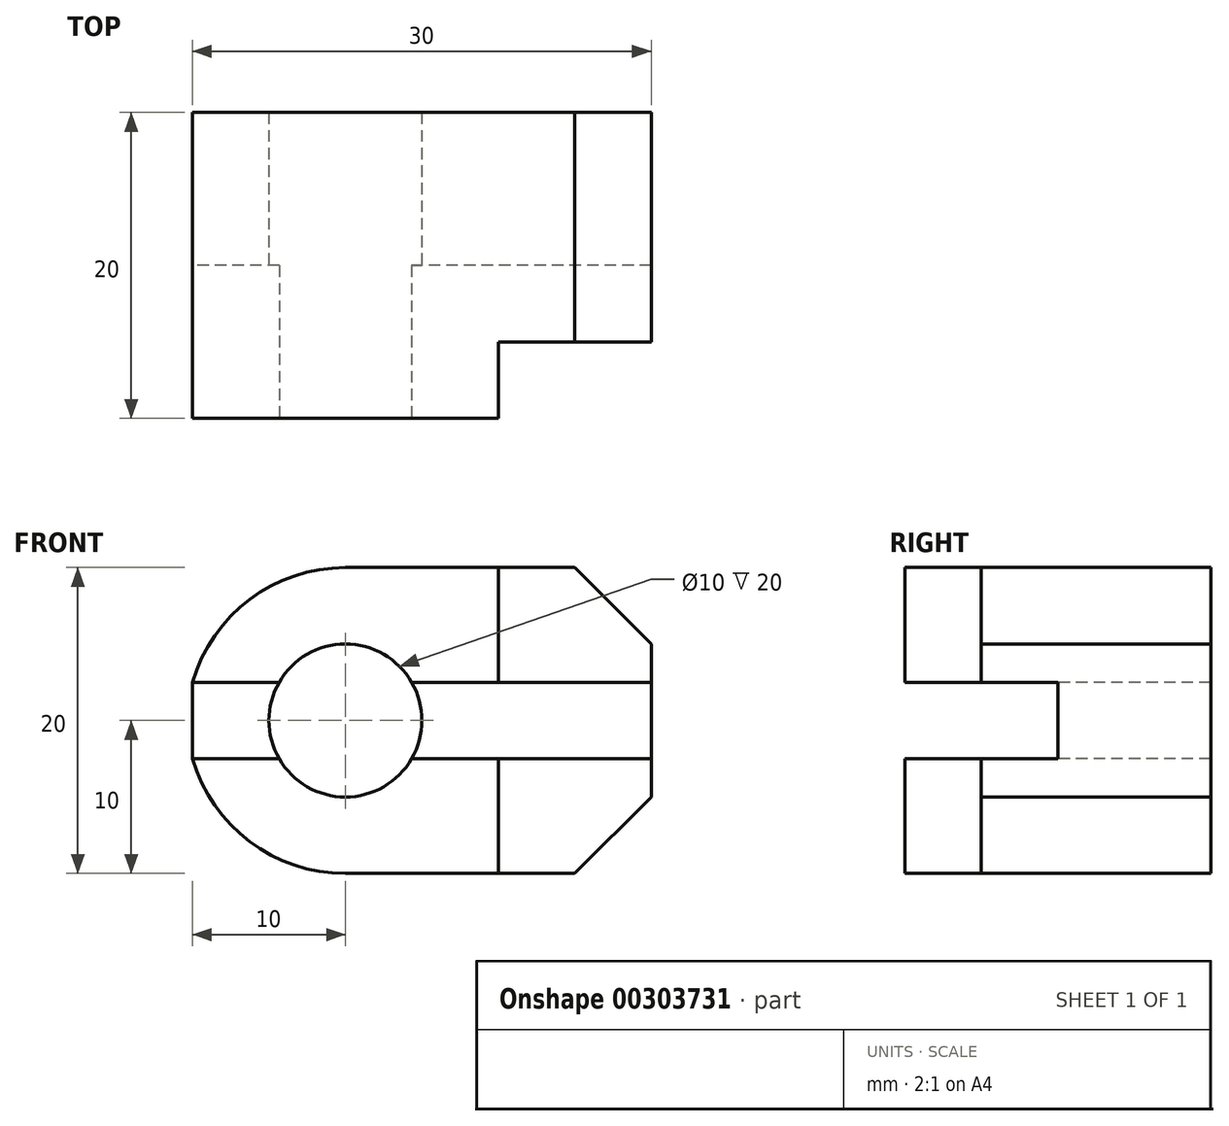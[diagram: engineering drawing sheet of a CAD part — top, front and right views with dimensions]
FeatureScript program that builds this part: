
annotation { "Feature Type Name" : "Feature", "Feature Type Description" : "" }
export const myFeature = defineFeature(function(context is Context, id is Id, definition is map)
    precondition{}
    {
        {
            var Q0;
            Q0=qCreatedBy(makeId("Top.planeOp"),FACE);
            var sketch = newSketch(context, id + "F0", { "sketchPlane" : qUnion([Q0])});
            skLineSegment(sketch, "E0", {"start": v(0, 0) * mm, "end": v(20, 0) * mm});
            skLineSegment(sketch, "E1", {"start": v(20, 0) * mm, "end": v(20, 5) * mm});
            skLineSegment(sketch, "E2", {"start": v(0, 0) * mm, "end": v(0, 20) * mm});
            skLineSegment(sketch, "E3", {"start": v(0, 20) * mm, "end": v(30, 20) * mm});
            skLineSegment(sketch, "E4", {"start": v(30, 20) * mm, "end": v(30, 5) * mm});
            skLineSegment(sketch, "E5", {"start": v(30, 5) * mm, "end": v(10, 5) * mm});
            skLineSegment(sketch, "E6", {"start": v(25, 20) * mm, "end": v(25, 5) * mm});
            skSolve(sketch);
        }
        {
            var Q0;
            Q0 = qSketchRegion(id + "F0", true);
            extrude(context, id + "F1", {"entities" : qUnion([Q0]), "endBound" : BoundingType.SYMMETRIC, "depth" : 20 * mm});
        }
        {
            var Q0;
            Q0=qCreatedBy(makeId("Front.planeOp"),FACE);
            var sketch = newSketch(context, id + "F2", { "sketchPlane" : qUnion([Q0])});
            skCircle(sketch, "E7", {"center": v(10, 0) * mm, "radius": 5 * mm});
            skPoint(sketch, "E8", {"position": v(10, 2.5) * mm});
            skPoint(sketch, "E9", {"position": v(10, -2.5) * mm});
            skLineSegment(sketch, "E10", {"start": v(5.67, 2.5) * mm, "end": v(0, 2.5) * mm});
            skLineSegment(sketch, "E11", {"start": v(5.67, -2.5) * mm, "end": v(0, -2.5) * mm});
            skLineSegment(sketch, "E12", {"start": v(14.33, 2.5) * mm, "end": v(20, 2.5) * mm});
            skLineSegment(sketch, "E13", {"start": v(14.33, -2.5) * mm, "end": v(20, -2.5) * mm});
            skLineSegment(sketch, "E14", {"start": v(14.33, 2.5) * mm, "end": v(30, 2.5) * mm});
            skLineSegment(sketch, "E15", {"start": v(14.33, -2.5) * mm, "end": v(30, -2.5) * mm});
            skArc(sketch, "E16", {"start": v(20, 2.5) * mm, "mid": v(10, 10) * mm, "end": v(0, 2.5) * mm});
            skPoint(sketch, "E17", {"position": v(10, -10) * mm});
            skArc(sketch, "E18", {"start": v(0, -2.5) * mm, "mid": v(10, -10) * mm, "end": v(20, -2.5) * mm});
            skLineSegment(sketch, "E19", {"start": v(10, 10) * mm, "end": v(0, 10) * mm});
            skLineSegment(sketch, "E20", {"start": v(0, 10) * mm, "end": v(0, 2.5) * mm});
            skLineSegment(sketch, "E21", {"start": v(10, -10) * mm, "end": v(0, -10) * mm});
            skLineSegment(sketch, "E22", {"start": v(0, -10) * mm, "end": v(0, -2.5) * mm});
            skLineSegment(sketch, "E23", {"start": v(0, 0) * mm, "end": v(35.65, 0) * mm, "construction": true});
            skLineSegment(sketch, "E24", {"start": v(30, 5) * mm, "end": v(30, -5) * mm});
            skPoint(sketch, "E25", {"position": v(30, 0) * mm});
            skLineSegment(sketch, "E26", {"start": v(30, 10) * mm, "end": v(25, 10) * mm});
            skLineSegment(sketch, "E27", {"start": v(25, -10) * mm, "end": v(30, -10) * mm});
            skLineSegment(sketch, "E28", {"start": v(25, 10) * mm, "end": v(30, 5) * mm});
            skLineSegment(sketch, "E29", {"start": v(25, -10) * mm, "end": v(30, -5) * mm});
            skLineSegment(sketch, "E30", {"start": v(30, 10) * mm, "end": v(30, 5) * mm});
            skLineSegment(sketch, "E31", {"start": v(30, -5) * mm, "end": v(30, -10) * mm});
            skSolve(sketch);
        }
        {
            var Q0;
            {var subQ2=sQuery(id+"F2.wireOp",EDGE,"E19");Q0=makeQuery(id+"F2.imprint","IMPRINT",FACE,{"disambiguationData":[TD([[makeQuery(id+"F2.imprint","IMPRINT",EDGE,{"derivedFrom":subQ2}),1.0]])]});}
            var Q1;
            {var subQ2=sQuery(id+"F2.wireOp",EDGE,"E21");Q1=makeQuery(id+"F2.imprint","IMPRINT",FACE,{"disambiguationData":[TD([[makeQuery(id+"F2.imprint","IMPRINT",EDGE,{"derivedFrom":subQ2}),-1.0]])]});}
            var Q2;
            Q2=makeQuery(id+"F2.imprint","IMPRINT",FACE,{"disambiguationData":[TD([[makeQuery(id+"F2.imprint","IMPRINT",EDGE,{"derivedFrom":sQuery(id+"F2.wireOp",EDGE,"E26")}),1.0]])]});
            var Q3;
            Q3=makeQuery(id+"F2.imprint","IMPRINT",FACE,{"disambiguationData":[TD([[makeQuery(id+"F2.imprint","IMPRINT",EDGE,{"derivedFrom":sQuery(id+"F2.wireOp",EDGE,"E27")}),1.0]])]});
            var Q4;
            {var subQ0=sQuery(id+"F2.wireOp",EDGE,"E7");var subQ1=makeQuery(id+"F2.imprint","INTERSECT",VERTEX,{"derivedFrom":[subQ0,sQuery(id+"F2.wireOp",EDGE,"E10")]});Q4=makeQuery(id+"F2.imprint","IMPRINT",FACE,{"disambiguationData":[TD([[makeQuery(id+"F2.imprint","IMPRINT",EDGE,{"disambiguationData":[TD([[subQ1,1.0]])],"derivedFrom":subQ0}),1.0]])]});}
            extrude(context, id + "F3", {"entities" : qUnion([Q0, Q1, Q2, Q3, Q4]), "operationType" : NewBodyOperationType.REMOVE, "endBound" : BoundingType.THROUGH_ALL, "oppositeDirection" : true, "depth" : 25 * mm});
        }
        {
            var Q0;
            Q0=qCreatedBy(makeId("Right.planeOp"),FACE);
            var sketch = newSketch(context, id + "F4", { "sketchPlane" : qUnion([Q0])});
            skLineSegment(sketch, "E32", {"start": v(0, 0) * mm, "end": v(61.43, 0) * mm, "construction": true});
            skLineSegment(sketch, "E33", {"start": v(10, 2.5) * mm, "end": v(0, 2.5) * mm});
            skLineSegment(sketch, "E34", {"start": v(10, -2.5) * mm, "end": v(0, -2.5) * mm});
            skLineSegment(sketch, "E35", {"start": v(0, -2.5) * mm, "end": v(0, 2.5) * mm});
            skPoint(sketch, "E36", {"position": v(10, 0) * mm});
            skLineSegment(sketch, "E37", {"start": v(10, -2.5) * mm, "end": v(10, 2.5) * mm});
            skSolve(sketch);
        }
        {
            var Q0;
            Q0 = qSketchRegion(id + "F4", true);
            extrude(context, id + "F5", {"entities" : qUnion([Q0]), "operationType" : NewBodyOperationType.REMOVE, "endBound" : BoundingType.THROUGH_ALL, "depth" : 25 * mm});
        }
    });
